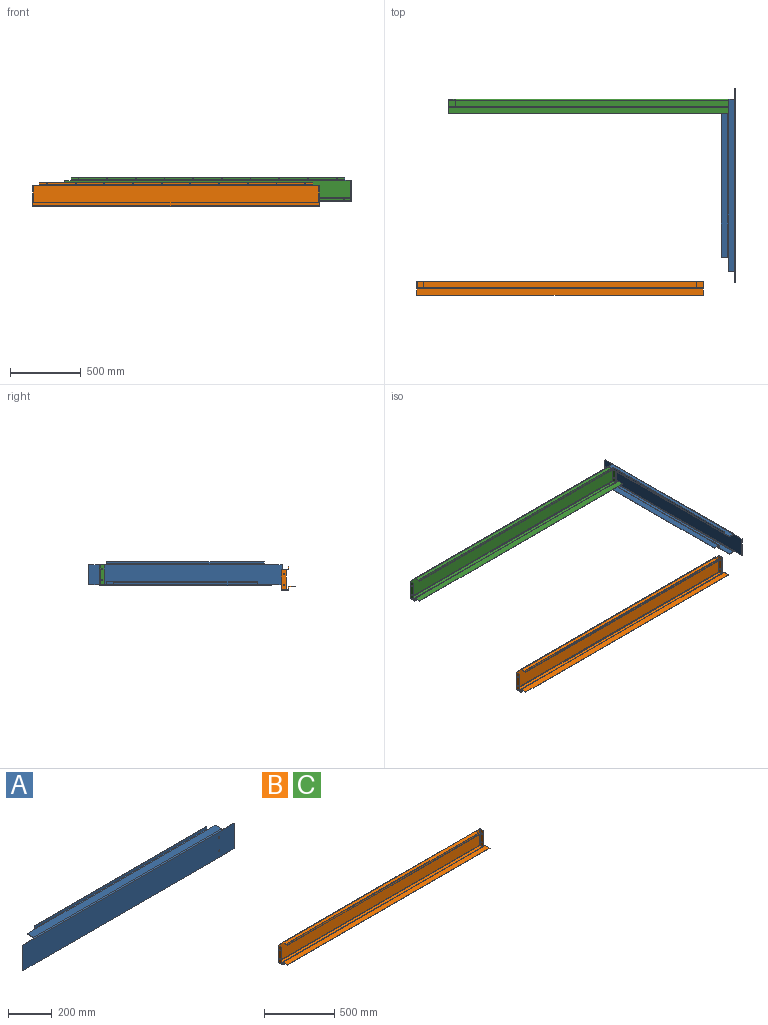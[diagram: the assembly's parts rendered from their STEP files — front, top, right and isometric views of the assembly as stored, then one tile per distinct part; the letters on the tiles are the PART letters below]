
ASSEMBLY  parts=3 mates=1
PART A: 56 faces, bbox 1371.6x101.6x168.8 mm
  f0: plane 142.51x2.66mm, normal (1,0,0), area 378.6mm2, adj f1,f7,f8,f9
  f1: plane 76.2x2.66mm, normal (0,0,-1), area 202.5mm2, adj f0,f8,f9,f53
  f2: plane 76.2x2.66mm, normal (0,0,-1), area 202.5mm2, adj f3,f8,f9,f52
  f3: plane 142.51x2.66mm, normal (-1,0,0), area 378.6mm2, adj f2,f4,f8,f9
  f4: plane 76.2x2.66mm, normal (0,0,1), area 202.5mm2, adj f3,f8,f9,f26
  f5: cylinder r=4.76mm len=9.53mm, axis (0,-1,0), area 79.5mm2, adj f8,f9
  f6: cylinder r=4.76mm len=9.53mm, axis (0,-1,0), area 79.5mm2, adj f8,f9
  f7: plane 76.2x2.66mm, normal (0,0,1), area 202.5mm2, adj f0,f8,f9,f25
  f8: plane 1371.6x142.51mm, normal (0,1,0), area 195330.1mm2, adj f0,f1,f2,f3,f4,f5,f6,f7
  f9: plane 1371.6x142.51mm, normal (0,-1,0), area 195330.1mm2, adj f0,f1,f2,f3,f4,f5,f6,f7
  f10: plane 50.8x2.66mm, normal (0,1,0), area 135mm2, adj f11,f14,f15,f22
  f11: plane 40.91x2.66mm, normal (1,0,0), area 108.7mm2, adj f10,f14,f15,f25
  f12: plane 40.91x2.66mm, normal (-1,0,0), area 108.7mm2, adj f13,f14,f15,f26
  f13: plane 50.8x2.66mm, normal (0,1,0), area 135mm2, adj f12,f14,f15,f21
  f14: plane 1219.2x40.91mm, normal (0,0,-1), area 49882.7mm2, adj f10,f11,f12,f13,f23,f28
  f15: plane 1219.2x40.91mm, normal (0,0,1), area 49882.7mm2, adj f10,f11,f12,f13,f24,f27
  f16: plane 1117.6x2.66mm, normal (0,0,1), area 2969.3mm2, adj f17,f18,f19,f20
  f17: plane 14.11x2.66mm, normal (1,0,0), area 37.5mm2, adj f16,f19,f20,f22
  f18: plane 14.11x2.66mm, normal (-1,0,0), area 37.5mm2, adj f16,f19,f20,f21
  f19: plane 1117.6x14.11mm, normal (0,1,0), area 15766.2mm2, adj f16,f17,f18,f23
  f20: plane 1117.6x14.11mm, normal (0,-1,0), area 15766.2mm2, adj f16,f17,f18,f24
  f21: plane 4.94x4.94mm, normal (-1,0,0), area 15.1mm2, adj f13,f18,f23,f24
  f22: plane 4.94x4.94mm, normal (1,0,0), area 15.1mm2, adj f10,f17,f23,f24
  f23: cylinder r=4.94mm len=1117.6mm, axis (-1,0,0), area 8677.3mm2, adj f14,f19,f21,f22
  f24: cylinder r=2.29mm len=1117.6mm, axis (-1,0,0), area 4013.1mm2, adj f15,f20,f21,f22
  f25: plane 4.94x4.94mm, normal (1,0,0), area 15.1mm2, adj f7,f11,f27,f28
  f26: plane 4.94x4.94mm, normal (-1,0,0), area 15.1mm2, adj f4,f12,f27,f28
  f27: cylinder r=4.94mm len=1219.2mm, axis (1,0,0), area 9466.1mm2, adj f9,f15,f25,f26
  f28: cylinder r=2.29mm len=1219.2mm, axis (1,0,0), area 4378mm2, adj f8,f14,f25,f26
  f29: plane 43.57x2.66mm, normal (-1,0,0), area 115.8mm2, adj f32,f33,f34,f52
  f30: plane 43.57x2.66mm, normal (1,0,0), area 115.8mm2, adj f31,f33,f34,f53
  f31: plane 101.6x2.66mm, normal (0,1,0), area 269.9mm2, adj f30,f33,f34,f49
  f32: plane 101.6x2.66mm, normal (0,1,0), area 269.9mm2, adj f29,f33,f34,f48
  f33: plane 1219.2x43.57mm, normal (0,0,1), area 53122mm2, adj f29,f30,f31,f32,f51,f55
  f34: plane 1219.2x43.57mm, normal (0,0,-1), area 53122mm2, adj f29,f30,f31,f32,f50,f54
  f35: plane 20.84x2.66mm, normal (1,0,0), area 55.4mm2, adj f37,f38,f44,f49
  f36: plane 20.84x2.66mm, normal (-1,0,0), area 55.4mm2, adj f37,f38,f45,f48
  f37: plane 1016x20.84mm, normal (0,-1,0), area 21171.6mm2, adj f35,f36,f46,f51
  f38: plane 1016x20.84mm, normal (0,1,0), area 21171.6mm2, adj f35,f36,f47,f50
  f39: plane 45.86x2.66mm, normal (1,0,0), area 121.8mm2, adj f40,f42,f43,f44
  f40: plane 1016x2.66mm, normal (0,1,0), area 2699.3mm2, adj f39,f41,f42,f43
  f41: plane 45.86x2.66mm, normal (-1,0,0), area 121.8mm2, adj f40,f42,f43,f45
  f42: plane 1016x45.86mm, normal (0,0,1), area 46590.9mm2, adj f39,f40,f41,f46
  f43: plane 1016x45.86mm, normal (0,0,-1), area 46590.9mm2, adj f39,f40,f41,f47
  f44: plane 4.94x4.94mm, normal (1,0,0), area 15.1mm2, adj f35,f39,f46,f47
  f45: plane 4.94x4.94mm, normal (-1,0,0), area 15.1mm2, adj f36,f41,f46,f47
  f46: cylinder r=4.94mm len=1016mm, axis (1,0,0), area 7888.4mm2, adj f37,f42,f44,f45
  f47: cylinder r=2.29mm len=1016mm, axis (1,0,0), area 3648.3mm2, adj f38,f43,f44,f45
  f48: plane 4.94x4.94mm, normal (-1,0,0), area 15.1mm2, adj f32,f36,f50,f51
  f49: plane 4.94x4.94mm, normal (1,0,0), area 15.1mm2, adj f31,f35,f50,f51
  f50: cylinder r=4.94mm len=1016mm, axis (-1,0,0), area 7888.4mm2, adj f34,f38,f48,f49
  f51: cylinder r=2.29mm len=1016mm, axis (-1,0,0), area 3648.3mm2, adj f33,f37,f48,f49
  f52: plane 4.94x4.94mm, normal (-1,0,0), area 15.1mm2, adj f2,f29,f54,f55
  f53: plane 4.94x4.94mm, normal (1,0,0), area 15.1mm2, adj f1,f30,f54,f55
  f54: cylinder r=4.94mm len=1219.2mm, axis (-1,0,0), area 9466.1mm2, adj f9,f34,f52,f53
  f55: cylinder r=2.29mm len=1219.2mm, axis (-1,0,0), area 4378mm2, adj f8,f33,f52,f53
PART B: 82 faces, bbox 2032x101.6x166.1 mm
  f0: plane 43.22x2.66mm, normal (0,0,1), area 114.8mm2, adj f2,f3,f27,f68
  f1: plane 43.22x2.66mm, normal (0,0,1), area 114.8mm2, adj f2,f3,f28,f78
  f2: plane 2022.11x139.85mm, normal (0,1,0), area 282787.3mm2, adj f0,f1,f29,f58,f69,f80
  f3: plane 2022.11x139.85mm, normal (0,-1,0), area 282787.3mm2, adj f0,f1,f30,f59,f70,f81
  f4: plane 43.57x2.66mm, normal (1,0,0), area 115.8mm2, adj f6,f7,f24,f27
  f5: plane 43.57x2.66mm, normal (-1,0,0), area 115.8mm2, adj f6,f7,f23,f28
  f6: plane 1935.68x43.57mm, normal (0,0,1), area 84340mm2, adj f4,f5,f26,f29
  f7: plane 1935.68x43.57mm, normal (0,0,-1), area 84340mm2, adj f4,f5,f25,f30
  f8: plane 1935.68x2.66mm, normal (0,0,1), area 5142.8mm2, adj f9,f20,f21,f22
  f9: plane 14.11x2.66mm, normal (1,0,0), area 37.5mm2, adj f8,f21,f22,f24
  f10: cylinder r=2.5mm len=5mm, axis (0,1,0), area 41.8mm2, adj f21,f22
  f11: cylinder r=2.5mm len=5mm, axis (0,1,0), area 41.8mm2, adj f21,f22
  f12: cylinder r=2.5mm len=5mm, axis (0,1,0), area 41.8mm2, adj f21,f22
  f13: cylinder r=2.5mm len=5mm, axis (0,1,0), area 41.8mm2, adj f21,f22
  f14: cylinder r=2.5mm len=5mm, axis (0,1,0), area 41.8mm2, adj f21,f22
  f15: cylinder r=2.5mm len=5mm, axis (0,1,0), area 41.8mm2, adj f21,f22
  f16: cylinder r=2.5mm len=5mm, axis (0,1,0), area 41.8mm2, adj f21,f22
  f17: cylinder r=2.5mm len=5mm, axis (0,1,0), area 41.8mm2, adj f21,f22
  f18: cylinder r=2.5mm len=5mm, axis (0,1,0), area 41.8mm2, adj f21,f22
  f19: cylinder r=2.5mm len=5mm, axis (0,1,0), area 41.8mm2, adj f21,f22
  f20: plane 14.11x2.66mm, normal (-1,0,0), area 37.5mm2, adj f8,f21,f22,f23
  f21: plane 1935.68x14.11mm, normal (0,1,0), area 27110.3mm2, adj f8,f9,f10,f11,f12,f13,f14,f15
  f22: plane 1935.68x14.11mm, normal (0,-1,0), area 27110.3mm2, adj f8,f9,f10,f11,f12,f13,f14,f15
  f23: plane 4.94x4.94mm, normal (-1,0,0), area 15.1mm2, adj f5,f20,f25,f26
  f24: plane 4.94x4.94mm, normal (1,0,0), area 15.1mm2, adj f4,f9,f25,f26
  f25: cylinder r=4.94mm len=1935.68mm, axis (-1,0,0), area 15029mm2, adj f7,f22,f23,f24
  f26: cylinder r=2.29mm len=1935.68mm, axis (-1,0,0), area 6950.7mm2, adj f6,f21,f23,f24
  f27: plane 4.94x4.94mm, normal (1,0,0), area 15.1mm2, adj f0,f4,f29,f30
  f28: plane 4.94x4.94mm, normal (-1,0,0), area 15.1mm2, adj f1,f5,f29,f30
  f29: cylinder r=4.94mm len=1935.68mm, axis (1,0,0), area 15029mm2, adj f2,f6,f27,f28
  f30: cylinder r=2.29mm len=1935.68mm, axis (1,0,0), area 6950.7mm2, adj f3,f7,f27,f28
  f31: plane 3.61x2.66mm, normal (0,1,0), area 9.6mm2, adj f33,f37,f38,f56
  f32: plane 43.57x2.66mm, normal (-1,0,0), area 115.8mm2, adj f33,f37,f38,f53
  f33: plane 2.66x1.33mm, normal (0,1,0), area 3.5mm2, adj f31,f32,f37,f38
  f34: plane 3.61x2.66mm, normal (0,1,0), area 9.6mm2, adj f35,f37,f38,f57
  f35: plane 2.66x1.33mm, normal (0,1,0), area 3.5mm2, adj f34,f36,f37,f38
  f36: plane 43.57x2.66mm, normal (1,0,0), area 115.8mm2, adj f35,f37,f38,f52
  f37: plane 2032x43.57mm, normal (0,0,-1), area 88536.6mm2, adj f31,f32,f33,f34,f35,f36,f54,f58
  f38: plane 2032x43.57mm, normal (0,0,1), area 88536.6mm2, adj f31,f32,f33,f34,f35,f36,f55,f59
  f39: plane 18.17x2.66mm, normal (-1,0,0), area 48.3mm2, adj f41,f42,f48,f53
  f40: plane 18.17x2.66mm, normal (1,0,0), area 48.3mm2, adj f41,f42,f49,f52
  f41: plane 2032x18.17mm, normal (0,-1,0), area 36923.8mm2, adj f39,f40,f51,f54
  f42: plane 2032x18.17mm, normal (0,1,0), area 36923.8mm2, adj f39,f40,f50,f55
  f43: plane 45.86x2.66mm, normal (-1,0,0), area 121.8mm2, adj f45,f46,f47,f48
  f44: plane 45.86x2.66mm, normal (1,0,0), area 121.8mm2, adj f45,f46,f47,f49
  f45: plane 2032x2.66mm, normal (0,-1,0), area 5398.7mm2, adj f43,f44,f46,f47
  f46: plane 2032x45.86mm, normal (0,0,-1), area 93181.7mm2, adj f43,f44,f45,f51
  f47: plane 2032x45.86mm, normal (0,0,1), area 93181.7mm2, adj f43,f44,f45,f50
  f48: plane 4.94x4.94mm, normal (-1,0,0), area 15.1mm2, adj f39,f43,f50,f51
  f49: plane 4.94x4.94mm, normal (1,0,0), area 15.1mm2, adj f40,f44,f50,f51
  f50: cylinder r=4.94mm len=2032mm, axis (-1,0,0), area 15776.8mm2, adj f42,f47,f48,f49
  f51: cylinder r=2.29mm len=2032mm, axis (-1,0,0), area 7296.6mm2, adj f41,f46,f48,f49
  f52: plane 4.94x4.94mm, normal (1,0,0), area 15.1mm2, adj f36,f40,f54,f55
  f53: plane 4.94x4.94mm, normal (-1,0,0), area 15.1mm2, adj f32,f39,f54,f55
  f54: cylinder r=4.94mm len=2032mm, axis (1,0,0), area 15776.8mm2, adj f37,f41,f52,f53
  f55: cylinder r=2.29mm len=2032mm, axis (1,0,0), area 7296.6mm2, adj f38,f42,f52,f53
  f56: plane 4.94x4.94mm, normal (-1,0,0), area 15.1mm2, adj f31,f58,f59,f79
  f57: plane 4.94x4.94mm, normal (1,0,0), area 15.1mm2, adj f34,f58,f59,f67
  f58: cylinder r=4.94mm len=2022.11mm, axis (-1,0,0), area 15700.1mm2, adj f2,f37,f56,f57
  f59: cylinder r=2.29mm len=2022.11mm, axis (-1,0,0), area 7261.1mm2, adj f3,f38,f56,f57
  f60: plane 30.62x2.66mm, normal (0,0,-1), area 81.3mm2, adj f64,f65,f66,f67
  f61: plane 30.62x2.66mm, normal (0,0,1), area 81.3mm2, adj f64,f65,f66,f68
  f62: cylinder r=4.76mm len=9.53mm, axis (1,0,0), area 79.5mm2, adj f65,f66
  f63: cylinder r=4.76mm len=9.53mm, axis (1,0,0), area 79.5mm2, adj f65,f66
  f64: plane 139.85x2.66mm, normal (0,-1,0), area 371.6mm2, adj f60,f61,f65,f66
  f65: plane 139.85x30.62mm, normal (1,0,0), area 4139.2mm2, adj f60,f61,f62,f63,f64,f69
  f66: plane 139.85x30.62mm, normal (-1,0,0), area 4139.2mm2, adj f60,f61,f62,f63,f64,f70
  f67: plane 4.94x4.94mm, normal (0,0,-1), area 15.1mm2, adj f57,f60,f69,f70
  f68: plane 4.94x4.94mm, normal (0,0,1), area 15.1mm2, adj f0,f61,f69,f70
  f69: cylinder r=4.94mm len=139.85mm, axis (0,0,-1), area 1085.8mm2, adj f2,f65,f67,f68
  f70: cylinder r=2.29mm len=139.85mm, axis (0,0,-1), area 502.2mm2, adj f3,f66,f67,f68
  f71: plane 30.62x2.66mm, normal (0,0,1), area 81.3mm2, adj f75,f76,f77,f78
  f72: plane 30.62x2.66mm, normal (0,0,-1), area 81.3mm2, adj f75,f76,f77,f79
  f73: cylinder r=4.76mm len=9.53mm, axis (-1,0,0), area 79.5mm2, adj f76,f77
  f74: cylinder r=4.76mm len=9.53mm, axis (-1,0,0), area 79.5mm2, adj f76,f77
  f75: plane 139.85x2.66mm, normal (0,-1,0), area 371.6mm2, adj f71,f72,f76,f77
  f76: plane 139.85x30.62mm, normal (-1,0,0), area 4139.2mm2, adj f71,f72,f73,f74,f75,f80
  f77: plane 139.85x30.62mm, normal (1,0,0), area 4139.2mm2, adj f71,f72,f73,f74,f75,f81
  f78: plane 4.94x4.94mm, normal (0,0,1), area 15.1mm2, adj f1,f71,f80,f81
  f79: plane 4.94x4.94mm, normal (0,0,-1), area 15.1mm2, adj f56,f72,f80,f81
  f80: cylinder r=4.94mm len=139.85mm, axis (0,0,1), area 1085.8mm2, adj f2,f76,f78,f79
  f81: cylinder r=2.29mm len=139.85mm, axis (0,0,1), area 502.2mm2, adj f3,f77,f78,f79
PART C: same geometry as B
PLACE A rot(axis=(0,0,1),90deg) t=(1098.38,-505.94,193.08)mm
PLACE B t=(-141.53,-1183.81,159.8)mm
PLACE C t=(82.38,103.66,194.42)mm fixed
MATE fastened A.f5 <-> C.f62  axis (-1,0,0) through (1098.38,83.41,157.65)mm
